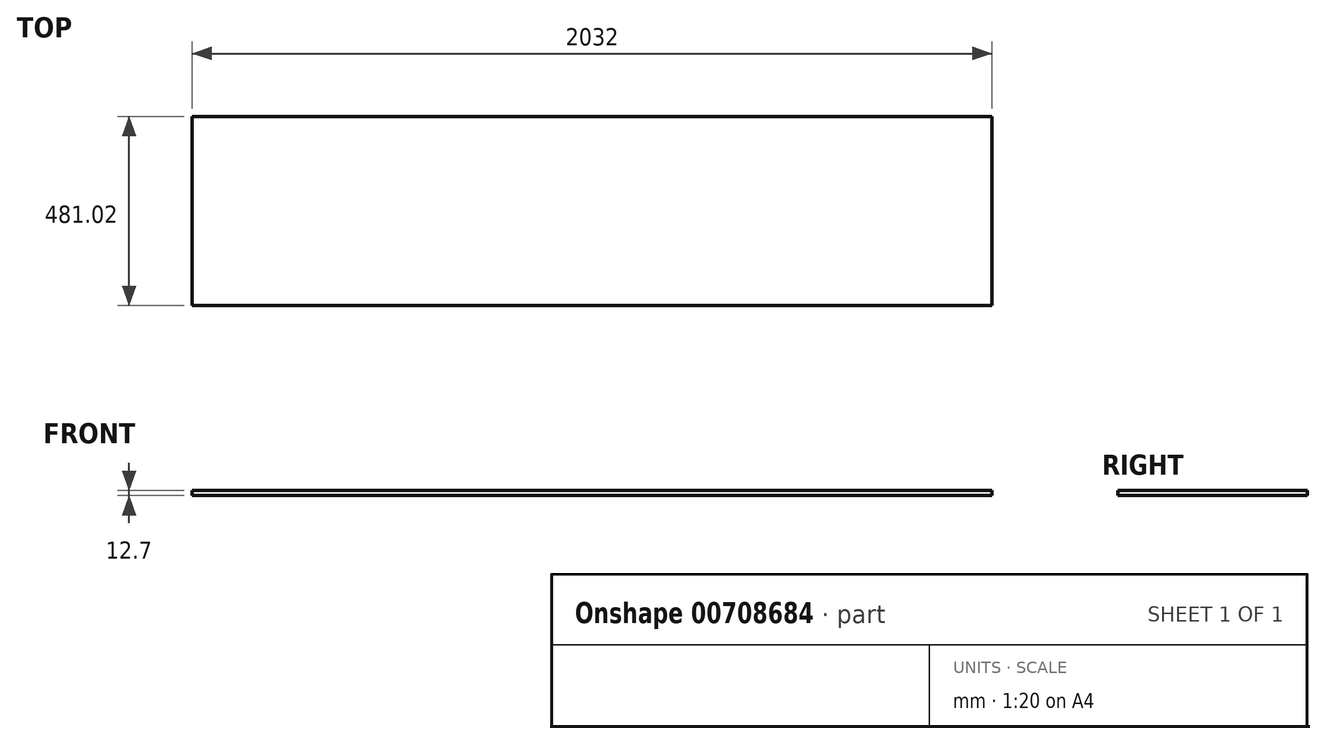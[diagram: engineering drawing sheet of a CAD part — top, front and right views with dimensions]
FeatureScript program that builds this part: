
annotation { "Feature Type Name" : "Feature", "Feature Type Description" : "" }
export const myFeature = defineFeature(function(context is Context, id is Id, definition is map)
    precondition{}
    {
        {
            var Q0;
            Q0=qCreatedBy(makeId("Top.planeOp"),FACE);
            var sketch = newSketch(context, id + "F0", { "sketchPlane" : qUnion([Q0])});
            skLineSegment(sketch, "E0.bottom", {"start": v(1016, -240.5) * mm, "end": v(-1016, -240.5) * mm});
            skLineSegment(sketch, "E0.top", {"start": v(1016, 240.5) * mm, "end": v(-1016, 240.5) * mm});
            skLineSegment(sketch, "E0.left", {"start": v(1016, -240.5) * mm, "end": v(1016, 240.5) * mm});
            skLineSegment(sketch, "E0.right", {"start": v(-1016, -240.5) * mm, "end": v(-1016, 240.5) * mm});
            skPoint(sketch, "E0.middle", {"position": v(0, 0) * mm});
            skSolve(sketch);
        }
        {
            var Q0;
            Q0=makeQuery(id+"F0.imprint","IMPRINT",FACE,{"disambiguationData":[TD([[makeQuery(id+"F0.imprint","IMPRINT",EDGE,{"derivedFrom":sQuery(id+"F0.wireOp",EDGE,"E0.bottom")}),-1.0]])]});
            extrude(context, id + "F1", {"entities" : qUnion([Q0]), "depth" : 12.7 * mm, "offsetDistance" : 25.4 * mm});
        }
    });
